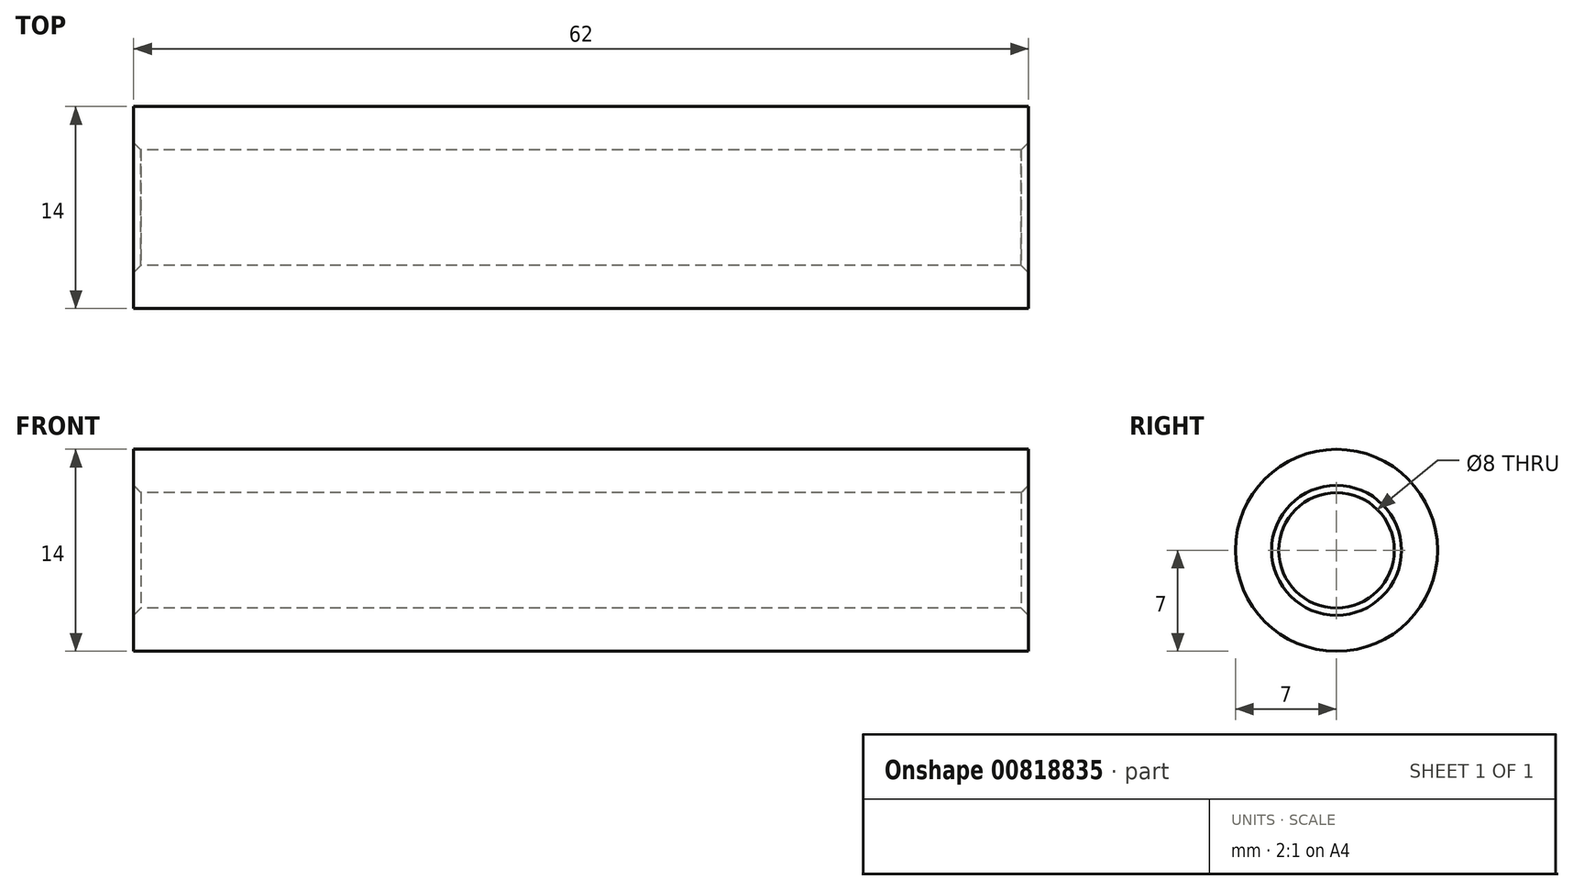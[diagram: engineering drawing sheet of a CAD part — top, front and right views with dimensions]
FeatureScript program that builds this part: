
annotation { "Feature Type Name" : "Feature", "Feature Type Description" : "" }
export const myFeature = defineFeature(function(context is Context, id is Id, definition is map)
    precondition{}
    {
        {
            var Q0;
            Q0=qCreatedBy(makeId("Front.planeOp"),FACE);
            var sketch = newSketch(context, id + "F0", { "sketchPlane" : qUnion([Q0])});
            skLineSegment(sketch, "E0.top", {"start": v(-31, 7) * mm, "end": v(31, 7) * mm});
            skLineSegment(sketch, "E0.left", {"start": v(-31, 4) * mm, "end": v(-31, 7) * mm});
            skLineSegment(sketch, "E0.right", {"start": v(31, 4) * mm, "end": v(31, 7) * mm});
            skLineSegment(sketch, "E1", {"start": v(-31, 4) * mm, "end": v(31, 4) * mm});
            skLineSegment(sketch, "E2", {"start": v(-50.47, 0) * mm, "end": v(62.06, 0) * mm, "construction": true});
            skSolve(sketch);
        }
        {
            var Q0;
            Q0=makeQuery(id+"F0.imprint","IMPRINT",FACE,{"disambiguationData":[TD([[makeQuery(id+"F0.imprint","IMPRINT",EDGE,{"derivedFrom":sQuery(id+"F0.wireOp",EDGE,"E0.top")}),-1.0]])]});
            var Q1;
            Q1=sQuery(id+"F0.wireOp",EDGE,"E2");
            revolve(context, id + "F1", {"surfaceOperationType" : NewSurfaceOperationType.NEW, "entities" : qUnion([Q0]), "axis" : qUnion([Q1]), "revolveType" : RevolveType.FULL});
        }
        {
            var Q0;
            Q0=makeQuery(id+"F1.opRevolve","SWEPT_EDGE",EDGE,{"disambiguationData":[OSD([sQuery(id+"F0.wireOp",EDGE,"E0.left"),sQuery(id+"F0.wireOp",EDGE,"E1")])]});
            var Q1;
            Q1=makeQuery(id+"F1.opRevolve","SWEPT_EDGE",EDGE,{"disambiguationData":[OSD([sQuery(id+"F0.wireOp",EDGE,"E0.right"),sQuery(id+"F0.wireOp",EDGE,"E1")])]});
            chamfer(context, id + "F2", {"entities" : qUnion([Q0, Q1]), "width" : 0.5 * mm, "tangentPropagation" : true});
        }
    });
